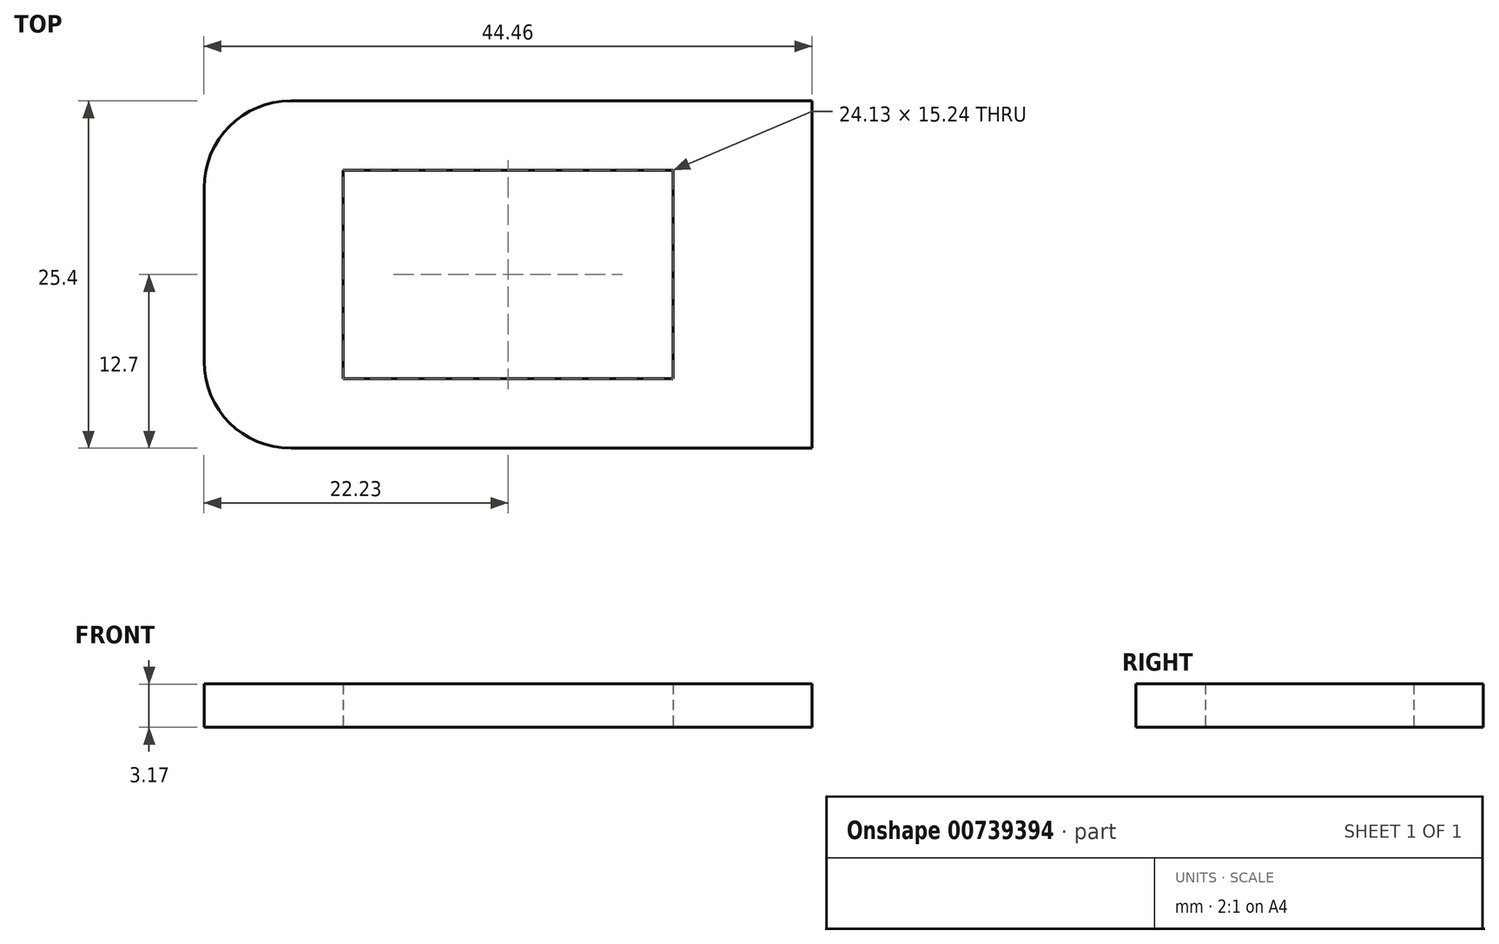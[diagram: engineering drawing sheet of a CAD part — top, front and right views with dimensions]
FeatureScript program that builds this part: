
annotation { "Feature Type Name" : "Feature", "Feature Type Description" : "" }
export const myFeature = defineFeature(function(context is Context, id is Id, definition is map)
    precondition{}
    {
        {
            var Q0;
            Q0=qCreatedBy(makeId("Top.planeOp"),FACE);
            var sketch = newSketch(context, id + "F0", { "sketchPlane" : qUnion([Q0])});
            skLineSegment(sketch, "E0.bottom", {"start": v(-15.87, -12.7) * mm, "end": v(22.23, -12.7) * mm});
            skLineSegment(sketch, "E0.top", {"start": v(-15.87, 12.7) * mm, "end": v(22.23, 12.7) * mm});
            skLineSegment(sketch, "E0.left", {"start": v(-22.22, -6.35) * mm, "end": v(-22.22, 6.35) * mm});
            skLineSegment(sketch, "E0.right", {"start": v(22.23, -12.7) * mm, "end": v(22.23, 12.7) * mm});
            skPoint(sketch, "E1.visualSharp", {"position": v(-22.22, 12.7) * mm});
            skArc(sketch, "E1.filletArc", {"start": v(-15.87, 12.7) * mm, "mid": v(-20.37, 10.84) * mm, "end": v(-22.22, 6.35) * mm});
            skPoint(sketch, "E2.visualSharp", {"position": v(-22.22, -12.7) * mm});
            skArc(sketch, "E2.filletArc", {"start": v(-22.22, -6.35) * mm, "mid": v(-20.37, -10.84) * mm, "end": v(-15.87, -12.7) * mm});
            skLineSegment(sketch, "E3.bottom", {"start": v(12.07, -7.62) * mm, "end": v(-12.06, -7.62) * mm});
            skLineSegment(sketch, "E3.top", {"start": v(12.07, 7.62) * mm, "end": v(-12.06, 7.62) * mm});
            skLineSegment(sketch, "E3.left", {"start": v(12.07, -7.62) * mm, "end": v(12.07, 7.62) * mm});
            skLineSegment(sketch, "E3.right", {"start": v(-12.06, -7.62) * mm, "end": v(-12.06, 7.62) * mm});
            skLineSegment(sketch, "E4", {"start": v(-12.06, -7.62) * mm, "end": v(12.07, 7.62) * mm, "construction": true});
            skLineSegment(sketch, "E5", {"start": v(-12.06, 7.62) * mm, "end": v(12.07, -7.62) * mm, "construction": true});
            skLineSegment(sketch, "E6", {"start": v(-22.22, 0) * mm, "end": v(22.23, 0) * mm, "construction": true});
            skPoint(sketch, "E7", {"position": v(-12.06, 0) * mm});
            skSolve(sketch);
        }
        {
            var Q0;
            Q0=makeQuery(id+"F0.imprint","IMPRINT",FACE,{"disambiguationData":[TD([[makeQuery(id+"F0.imprint","IMPRINT",EDGE,{"derivedFrom":sQuery(id+"F0.wireOp",EDGE,"E0.bottom")}),1.0]])]});
            extrude(context, id + "F1", {"entities" : qUnion([Q0]), "depth" : 3.17 * mm, "offsetDistance" : 25.4 * mm});
        }
    });
